# Revit family: EL_Peron
name_source: partatom
category: Lighting Fixtures
units: mm (PartAtom-declared; Revit-internal decimal feet)

## family parameters
Always vertical = Yes
Cut with Voids When Loaded = No
Light Source = Yes
Maintain Annotation Orientation = No
OmniClass Number = 23.80.70.00
OmniClass Title = Lighting
Part Type = Normal
Room Calculation Point = No
Round Connector Dimension = Use Diameter
Shared = No
Work Plane-Based = No

## types (13) — shared parameters
CE Conformity = CE Mark
Color Filter = 16777215
Control Gear = LED Driver
Default Elevation = 1500 mm
Description = Street luminaire
Diffuser Material  = Flat glass
Dimming Lamp Color Temperature Shift = <None>
EL_Voltage = AC 220V - 240V / 50-60Hz
Emit from Line Length = 610 mm
Housing Height = 89 mm  [stored 0.291995 ft]
Housing Width = 160 mm  [stored 0.524934 ft]
IK = IK10
IP = IP66
Lamp = LED
Life Time = 100 000 h
Light Source Symbol Length = 3048 mm  [stored 10 ft]
Luminaire Material = Kov
Manufacturer = ELEKTRO-LUMEN, s. r. o.
Spot Beam Angle = 30.00°
Spot Field Angle = 90.00°
Terminal Block Poles = 2, 3, 5
Tilt Angle = 90.00°
URL Luminaire = https://www.el-lumen.cz
URL Manufacturer = https://www.el-lumen.cz
Voltage  = AC 220V - 240V / 50-60Hz

## per-type parameters (varying)
| type | CCT | CRI | Housing Length | Luminaire Type | Luminous Flux of LED | Luminous Flux of Luminaire | Model | Optical Efficacy | Power | Weight |
| PERON 4 Uxx  12k0 740 B124 | 4000 | 70 | 1045 mm  [stored 3.42848 ft] | PERON 4 | 12000 lm | 9708 lm | PERON 4 | 80.9 | 64 W | 8.5 |
| PERON 4 Uxx  10k0 740 B124 | 4000 | 70 | 1045 mm  [stored 3.42848 ft] | PERON 4 | 10000 lm | 8090 lm | PERON 4 | 80.9 | 53 W | 8.5 |
| PERON 4 Uxx  8k0 740 B124 | 4000 | 70 | 1045 mm  [stored 3.42848 ft] | PERON 4 | 8000 lm | 6472 lm | PERON 4 | 80.9 | 42 W | 8.5 |
| PERON 4 Uxx  12k0 730 B124 | 3000 | 70 | 1045 mm  [stored 3.42848 ft] | PERON 4 | 12000 lm | 9708 lm | PERON 4 | 80.9 | 68 W | 8.5 |
| PERON 4 Uxx  10k0 730 B124 | 3000 | 70 | 1045 mm  [stored 3.42848 ft] | PERON 4 | 10000 lm | 8090 lm | PERON 4 | 80.9 | 56 W | 8.5 |
| PERON 4 Uxx  8k0 730 B124 | 3000 | 70 | 1045 mm  [stored 3.42848 ft] | PERON 4 | 8000 lm | 6472 lm | PERON 4 | 80.9 | 44 W | 8.5 |
| PERON 3 Uxx  6k0 740 B124 | 4000 | 70 | 810 mm  [stored 2.65748 ft] | PERON 3 | 6000 lm | 4854 lm | PERON 3 | 80.9 | 32 W | 6.5 |
| PERON 3 Uxx  4k0 740 B124 | 4000 | 70 | 810 mm  [stored 2.65748 ft] | PERON 3 | 4000 lm | 3236 lm | PERON 3 | 80.9 | 21 W | 6.5 |
| PERON 3 Uxx  2k6 740 B124 | 4000 | 70 | 810 mm  [stored 2.65748 ft] | PERON 3 | 2600 lm | 2103 lm | PERON 3 | 80.9 | 14 W | 6.5 |
| PERON 3 Uxx  6k0 730 B124 | 3000 | 70 | 810 mm  [stored 2.65748 ft] | PERON 3 | 6000 lm | 4854 lm | PERON 3 | 80.9 | 33 W | 6.5 |
| PERON 3 Uxx  4k0 730 B124 | 3000 | 70 | 810 mm  [stored 2.65748 ft] | PERON 3 | 4000 lm | 3236 lm | PERON 3 | 80.9 | 22 W | 6.5 |
| PERON 3 Uxx  2k6 730 B124 | 3000 | 70 | 810 mm  [stored 2.65748 ft] | PERON 3 | 2600 lm | 2103 lm | PERON 3 | 80.9 | 15 W | 6.5 |
| PERON 2 | 0 | 0 | 575 mm  [stored 1.88648 ft] | PERON 2 | 0 lm | 0 lm | PERON 2 | 0 | 0 W | 0 |

note: column(s) folded — value = type name in every type: Luminaire Model

note: [stored X ft] marks values corroborated as IEEE doubles in the binary element streams (Revit-internal decimal feet)
